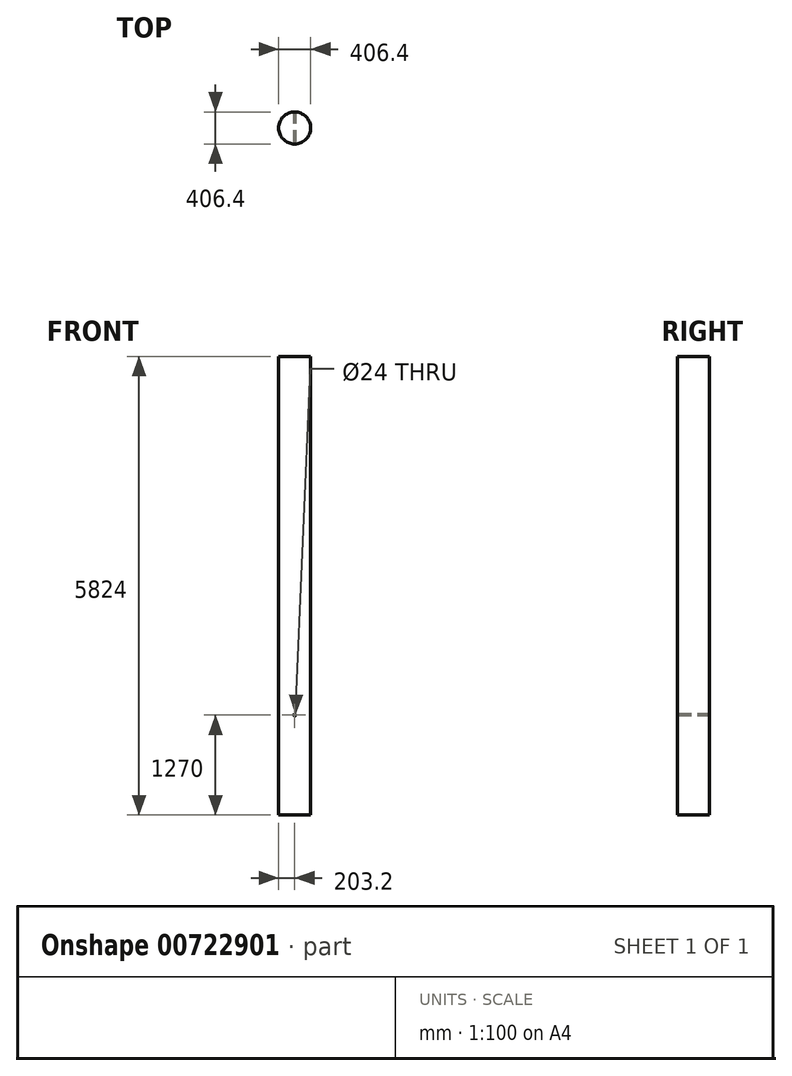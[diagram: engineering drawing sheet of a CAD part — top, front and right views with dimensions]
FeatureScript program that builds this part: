
annotation { "Feature Type Name" : "Feature", "Feature Type Description" : "" }
export const myFeature = defineFeature(function(context is Context, id is Id, definition is map)
    precondition{}
    {
        {
            var Q0;
            Q0=qCreatedBy(makeId("Top.planeOp"),FACE);
            var sketch = newSketch(context, id + "F0", { "sketchPlane" : qUnion([Q0])});
            skCircle(sketch, "E0", {"center": v(0, 0) * mm, "radius": 203.2 * mm});
            skSolve(sketch);
        }
        {
            var Q0;
            Q0=makeQuery(id+"F0.imprint","IMPRINT",FACE,{"disambiguationData":[TD([[makeQuery(id+"F0.imprint","IMPRINT",EDGE,{"derivedFrom":sQuery(id+"F0.wireOp",EDGE,"E0")}),1.0]])]});
            extrude(context, id + "F1", {"entities" : qUnion([Q0]), "depth" : (5870 - 30 - 16) * mm, "offsetDistance" : 25 * mm});
        }
        {
            var Q0;
            Q0=qCreatedBy(makeId("Front.planeOp"),FACE);
            var sketch = newSketch(context, id + "F2", { "sketchPlane" : qUnion([Q0])});
            skCircle(sketch, "E1", {"center": v(0, 1270) * mm, "radius": 12 * mm});
            skSolve(sketch);
        }
        {
            var Q0;
            Q0 = qSketchRegion(id + "F2", true);
            extrude(context, id + "F3", {"entities" : qUnion([Q0]), "operationType" : NewBodyOperationType.REMOVE, "endBound" : BoundingType.SYMMETRIC, "oppositeDirection" : true, "depth" : 406.4 * mm, "offsetDistance" : 25 * mm});
        }
    });
